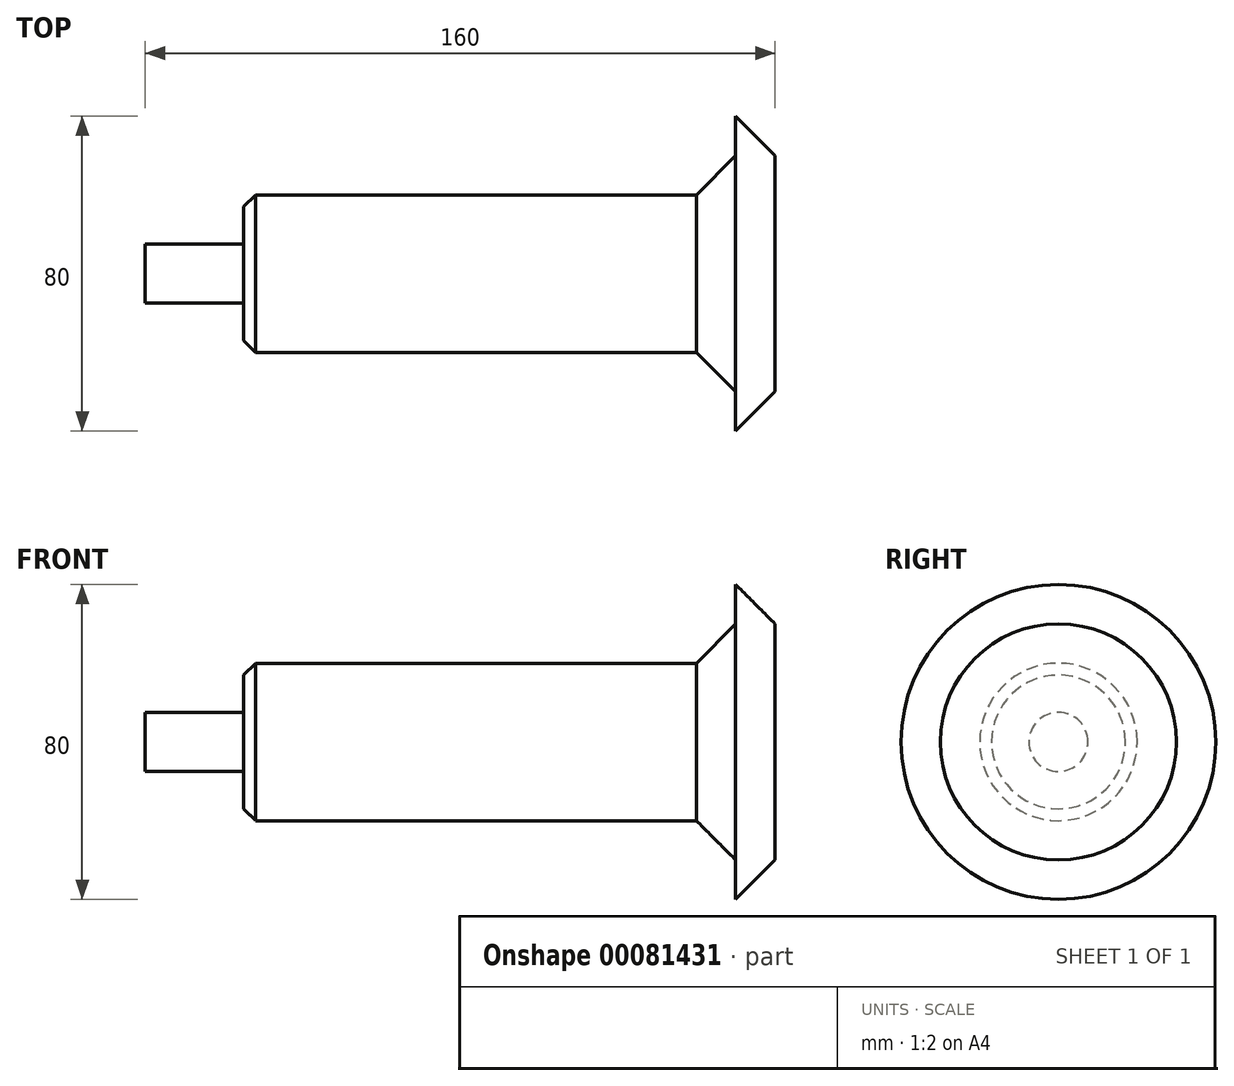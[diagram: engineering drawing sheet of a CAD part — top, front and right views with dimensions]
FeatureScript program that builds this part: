
annotation { "Feature Type Name" : "Feature", "Feature Type Description" : "" }
export const myFeature = defineFeature(function(context is Context, id is Id, definition is map)
    precondition{}
    {
        {
            var Q0;
            Q0=qCreatedBy(makeId("Front.planeOp"),FACE);
            var sketch = newSketch(context, id + "F0", { "sketchPlane" : qUnion([Q0])});
            skLineSegment(sketch, "E0", {"start": v(0, 0) * mm, "end": v(-147.67, 0) * mm, "construction": true});
            skLineSegment(sketch, "E1", {"start": v(0, 40) * mm, "end": v(-10, 40) * mm});
            skLineSegment(sketch, "E2", {"start": v(-10, 40) * mm, "end": v(-10, 20) * mm});
            skLineSegment(sketch, "E3", {"start": v(-10, 20) * mm, "end": v(-135, 20) * mm});
            skLineSegment(sketch, "E4", {"start": v(-135, 20) * mm, "end": v(-135, 7.5) * mm});
            skLineSegment(sketch, "E5", {"start": v(-135, 7.5) * mm, "end": v(-160, 7.5) * mm});
            skLineSegment(sketch, "E6", {"start": v(-160, 7.5) * mm, "end": v(-160, 0) * mm});
            skLineSegment(sketch, "E7", {"start": v(-160, 0) * mm, "end": v(0, 0) * mm});
            skLineSegment(sketch, "E8", {"start": v(0, 40) * mm, "end": v(0, 0) * mm});
            skSolve(sketch);
        }
        {
            var Q0;
            Q0=makeQuery(id+"F0.imprint","IMPRINT",FACE,{"disambiguationData":[TD([[makeQuery(id+"F0.imprint","IMPRINT",EDGE,{"derivedFrom":sQuery(id+"F0.wireOp",EDGE,"E1")}),1.0]])]});
            var Q1;
            Q1=sQuery(id+"F0.wireOp",EDGE,"E7");
            revolve(context, id + "F1", {"entities" : qUnion([Q0]), "axis" : qUnion([Q1]), "revolveType" : RevolveType.FULL});
        }
        {
            var Q0;
            Q0=makeQuery(id+"F1.opRevolve","SWEPT_FACE",FACE,{"disambiguationData":[OSD([sQuery(id+"F0.wireOp",EDGE,"E8")])]});
            chamfer(context, id + "F2", {"entities" : qUnion([Q0]), "width" : 10 * mm, "tangentPropagation" : true});
        }
        {
            var Q0;
            Q0=makeQuery(id+"F1.opRevolve","SWEPT_EDGE",EDGE,{"disambiguationData":[OSD([sQuery(id+"F0.wireOp",EDGE,"E2"),sQuery(id+"F0.wireOp",EDGE,"E3")])]});
            chamfer(context, id + "F3", {"entities" : qUnion([Q0]), "width" : 10 * mm, "tangentPropagation" : true});
        }
        {
            var Q0;
            Q0=makeQuery(id+"F1.opRevolve","SWEPT_EDGE",EDGE,{"disambiguationData":[OSD([sQuery(id+"F0.wireOp",EDGE,"E3"),sQuery(id+"F0.wireOp",EDGE,"E4")])]});
            chamfer(context, id + "F4", {"entities" : qUnion([Q0]), "width" : 3 * mm, "tangentPropagation" : true});
        }
    });
